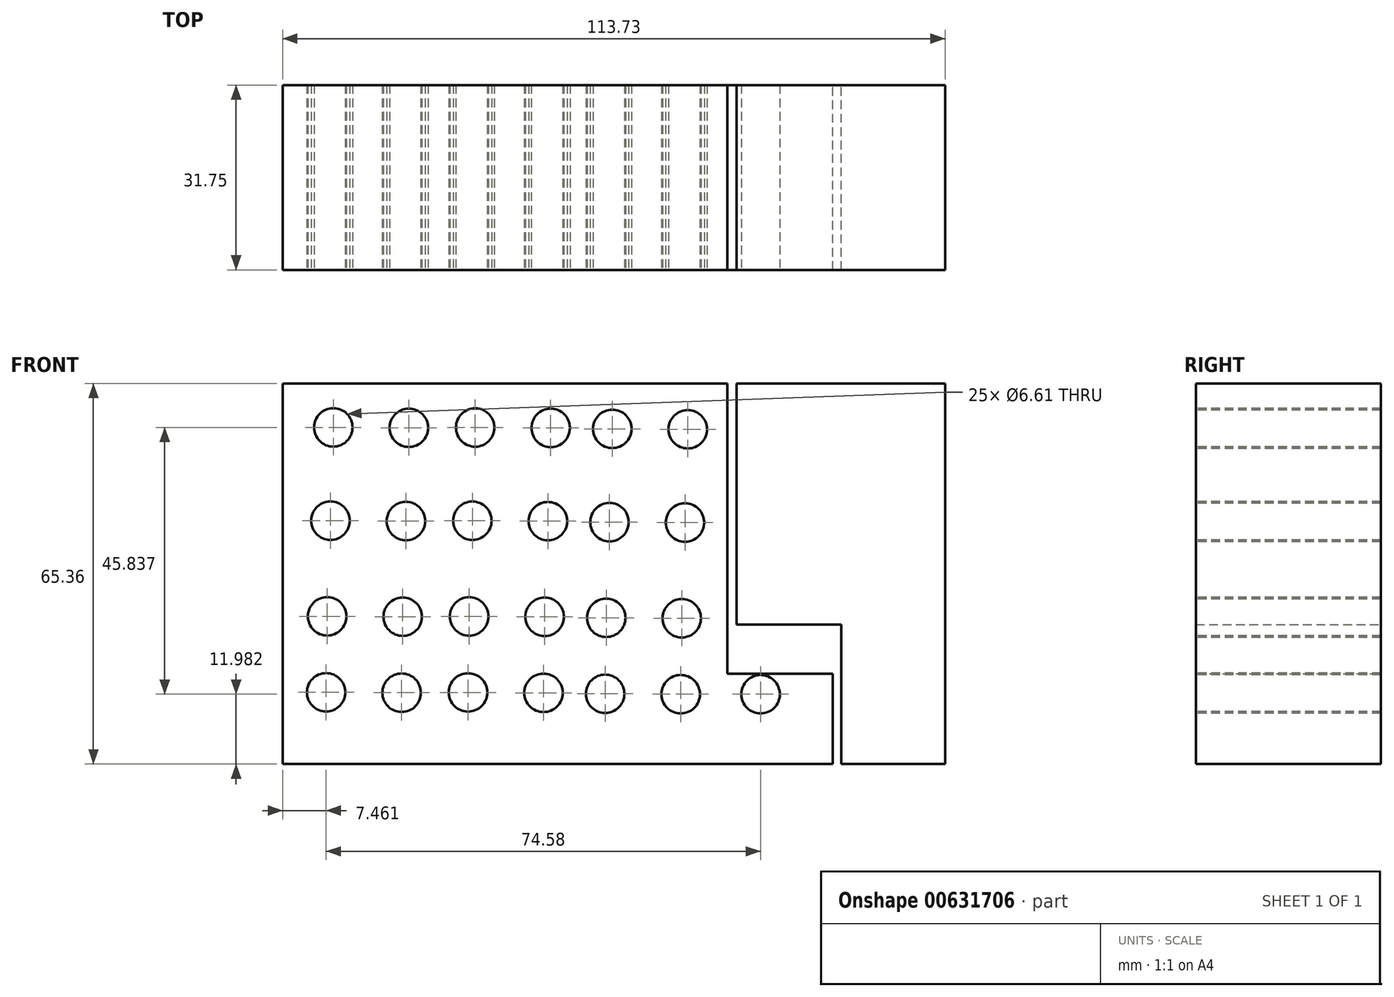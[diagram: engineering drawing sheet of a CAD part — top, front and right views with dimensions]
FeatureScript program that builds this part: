
annotation { "Feature Type Name" : "Feature", "Feature Type Description" : "" }
export const myFeature = defineFeature(function(context is Context, id is Id, definition is map)
    precondition{}
    {
        {
            var Q0;
            Q0=qCreatedBy(makeId("Front.planeOp"),FACE);
            var sketch = newSketch(context, id + "F0", { "sketchPlane" : qUnion([Q0])});
            skLineSegment(sketch, "E0.bottom", {"start": v(0, 0) * mm, "end": v(76.36, 0) * mm});
            skLineSegment(sketch, "E0.top", {"start": v(0, 65.36) * mm, "end": v(76.36, 65.36) * mm});
            skLineSegment(sketch, "E0.left", {"start": v(0, 0) * mm, "end": v(0, 65.36) * mm});
            skLineSegment(sketch, "E0.right", {"start": v(76.36, 0) * mm, "end": v(76.36, 65.36) * mm});
            skLineSegment(sketch, "E1", {"start": v(76.36, 0) * mm, "end": v(95.87, 0) * mm});
            skLineSegment(sketch, "E2", {"start": v(95.87, 0) * mm, "end": v(95.87, 15.7) * mm});
            skLineSegment(sketch, "E3", {"start": v(76.36, 65.36) * mm, "end": v(77.94, 65.36) * mm});
            skLineSegment(sketch, "E4", {"start": v(77.94, 65.36) * mm, "end": v(77.94, 23.98) * mm});
            skLineSegment(sketch, "E5", {"start": v(77.94, 23.98) * mm, "end": v(95.86, 23.98) * mm});
            skLineSegment(sketch, "E6", {"start": v(95.86, 23.98) * mm, "end": v(95.87, 15.7) * mm});
            skLineSegment(sketch, "E7", {"start": v(77.94, 65.36) * mm, "end": v(113.73, 65.36) * mm});
            skLineSegment(sketch, "E8", {"start": v(113.73, 65.36) * mm, "end": v(113.73, 0) * mm});
            skLineSegment(sketch, "E9", {"start": v(113.73, 0) * mm, "end": v(95.87, 0) * mm});
            skLineSegment(sketch, "E10", {"start": v(94.47, 0) * mm, "end": v(94.47, 15.5) * mm});
            skLineSegment(sketch, "E11", {"start": v(94.47, 15.5) * mm, "end": v(76.36, 15.5) * mm});
            skSolve(sketch);
        }
        {
            var Q0;
            {var subQ1=sQuery(id+"F0.wireOp",EDGE,"E0.bottom");Q0=makeQuery(id+"F0.imprint","IMPRINT",FACE,{"disambiguationData":[TD([[makeQuery(id+"F0.imprint","IMPRINT",EDGE,{"derivedFrom":subQ1}),1.0]])]});}
            var Q1;
            {var subQ0=sQuery(id+"F0.wireOp",EDGE,"E1");Q1=makeQuery(id+"F0.imprint","IMPRINT",FACE,{"disambiguationData":[TD([[makeQuery(id+"F0.imprint","IMPRINT",EDGE,{"derivedFrom":subQ0}),1.0]])]});}
            extrude(context, id + "F1", {"entities" : qUnion([Q0, Q1]), "depth" : 31.75 * mm, "offsetDistance" : 25.4 * mm});
        }
        {
            var Q0;
            Q0=makeQuery(id+"F1.opExtrude","CAP_FACE",FACE,{"disambiguationData":[OSD([sQuery(id+"F0.wireOp",EDGE,"E0.bottom"),sQuery(id+"F0.wireOp",EDGE,"E0.top"),sQuery(id+"F0.wireOp",EDGE,"E0.left"),sQuery(id+"F0.wireOp",EDGE,"E0.right"),sQuery(id+"F0.wireOp",EDGE,"E1"),sQuery(id+"F0.wireOp",EDGE,"E2"),sQuery(id+"F0.wireOp",EDGE,"N7w3tQHg-34Xs-ULp0-82r7-44mW0SfcWPOa")])],"isStart":false});
            var sketch = newSketch(context, id + "F2", { "sketchPlane" : qUnion([Q0])});
            skCircle(sketch, "E12", {"center": v(8.7, 57.82) * mm, "radius": 3.3 * mm});
            skCircle(sketch, "E13", {"center": v(21.66, 57.75) * mm, "radius": 3.3 * mm});
            skCircle(sketch, "E14", {"center": v(33.05, 57.8) * mm, "radius": 3.3 * mm});
            skCircle(sketch, "E15", {"center": v(46.02, 57.74) * mm, "radius": 3.3 * mm});
            skCircle(sketch, "E16", {"center": v(56.6, 57.56) * mm, "radius": 3.3 * mm});
            skCircle(sketch, "E17", {"center": v(69.55, 57.5) * mm, "radius": 3.3 * mm});
            skCircle(sketch, "E18", {"center": v(8.2, 41.8) * mm, "radius": 3.3 * mm});
            skCircle(sketch, "E19", {"center": v(21.17, 41.72) * mm, "radius": 3.3 * mm});
            skCircle(sketch, "E20", {"center": v(32.57, 41.78) * mm, "radius": 3.3 * mm});
            skCircle(sketch, "E21", {"center": v(45.53, 41.7) * mm, "radius": 3.3 * mm});
            skCircle(sketch, "E22", {"center": v(56.1, 41.54) * mm, "radius": 3.3 * mm});
            skCircle(sketch, "E23", {"center": v(69.07, 41.47) * mm, "radius": 3.3 * mm});
            skCircle(sketch, "E24", {"center": v(7.65, 25.37) * mm, "radius": 3.3 * mm});
            skCircle(sketch, "E25", {"center": v(20.61, 25.3) * mm, "radius": 3.3 * mm});
            skCircle(sketch, "E26", {"center": v(32.01, 25.35) * mm, "radius": 3.3 * mm});
            skCircle(sketch, "E27", {"center": v(44.97, 25.28) * mm, "radius": 3.3 * mm});
            skCircle(sketch, "E28", {"center": v(55.55, 25.11) * mm, "radius": 3.3 * mm});
            skCircle(sketch, "E29", {"center": v(68.51, 25.04) * mm, "radius": 3.3 * mm});
            skCircle(sketch, "E30", {"center": v(7.46, 12.3) * mm, "radius": 3.3 * mm});
            skCircle(sketch, "E31", {"center": v(20.42, 12.24) * mm, "radius": 3.3 * mm});
            skCircle(sketch, "E32", {"center": v(31.82, 12.3) * mm, "radius": 3.3 * mm});
            skCircle(sketch, "E33", {"center": v(44.79, 12.22) * mm, "radius": 3.3 * mm});
            skCircle(sketch, "E34", {"center": v(55.36, 12.05) * mm, "radius": 3.3 * mm});
            skCircle(sketch, "E35", {"center": v(68.32, 11.98) * mm, "radius": 3.3 * mm});
            skCircle(sketch, "E36", {"center": v(82.04, 11.98) * mm, "radius": 3.3 * mm});
            skSolve(sketch);
        }
        {
            var Q0;
            Q0=makeQuery(id+"F2.imprint","IMPRINT",FACE,{"disambiguationData":[TD([[makeQuery(id+"F2.imprint","IMPRINT",EDGE,{"derivedFrom":sQuery(id+"F2.wireOp",EDGE,"E25")}),1.0]])]});
            var Q1;
            Q1=makeQuery(id+"F2.imprint","IMPRINT",FACE,{"disambiguationData":[TD([[makeQuery(id+"F2.imprint","IMPRINT",EDGE,{"derivedFrom":sQuery(id+"F2.wireOp",EDGE,"E26")}),1.0]])]});
            var Q2;
            Q2=makeQuery(id+"F2.imprint","IMPRINT",FACE,{"disambiguationData":[TD([[makeQuery(id+"F2.imprint","IMPRINT",EDGE,{"derivedFrom":sQuery(id+"F2.wireOp",EDGE,"E27")}),1.0]])]});
            var Q3;
            Q3=makeQuery(id+"F2.imprint","IMPRINT",FACE,{"disambiguationData":[TD([[makeQuery(id+"F2.imprint","IMPRINT",EDGE,{"derivedFrom":sQuery(id+"F2.wireOp",EDGE,"E28")}),1.0]])]});
            var Q4;
            Q4=makeQuery(id+"F2.imprint","IMPRINT",FACE,{"disambiguationData":[TD([[makeQuery(id+"F2.imprint","IMPRINT",EDGE,{"derivedFrom":sQuery(id+"F2.wireOp",EDGE,"E30")}),1.0]])]});
            var Q5;
            Q5=makeQuery(id+"F2.imprint","IMPRINT",FACE,{"disambiguationData":[TD([[makeQuery(id+"F2.imprint","IMPRINT",EDGE,{"derivedFrom":sQuery(id+"F2.wireOp",EDGE,"E32")}),1.0]])]});
            var Q6;
            Q6=makeQuery(id+"F2.imprint","IMPRINT",FACE,{"disambiguationData":[TD([[makeQuery(id+"F2.imprint","IMPRINT",EDGE,{"derivedFrom":sQuery(id+"F2.wireOp",EDGE,"E34")}),1.0]])]});
            var Q7;
            Q7=makeQuery(id+"F2.imprint","IMPRINT",FACE,{"disambiguationData":[TD([[makeQuery(id+"F2.imprint","IMPRINT",EDGE,{"derivedFrom":sQuery(id+"F2.wireOp",EDGE,"E29")}),1.0]])]});
            var Q8;
            Q8=makeQuery(id+"F2.imprint","IMPRINT",FACE,{"disambiguationData":[TD([[makeQuery(id+"F2.imprint","IMPRINT",EDGE,{"derivedFrom":sQuery(id+"F2.wireOp",EDGE,"E31")}),1.0]])]});
            var Q9;
            Q9=makeQuery(id+"F2.imprint","IMPRINT",FACE,{"disambiguationData":[TD([[makeQuery(id+"F2.imprint","IMPRINT",EDGE,{"derivedFrom":sQuery(id+"F2.wireOp",EDGE,"E33")}),1.0]])]});
            var Q10;
            Q10=makeQuery(id+"F2.imprint","IMPRINT",FACE,{"disambiguationData":[TD([[makeQuery(id+"F2.imprint","IMPRINT",EDGE,{"derivedFrom":sQuery(id+"F2.wireOp",EDGE,"E35")}),1.0]])]});
            var Q11;
            Q11=makeQuery(id+"F2.imprint","IMPRINT",FACE,{"disambiguationData":[TD([[makeQuery(id+"F2.imprint","IMPRINT",EDGE,{"derivedFrom":sQuery(id+"F2.wireOp",EDGE,"E24")}),1.0]])]});
            var Q12;
            Q12=makeQuery(id+"F2.imprint","IMPRINT",FACE,{"disambiguationData":[TD([[makeQuery(id+"F2.imprint","IMPRINT",EDGE,{"derivedFrom":sQuery(id+"F2.wireOp",EDGE,"E23")}),1.0]])]});
            var Q13;
            Q13=makeQuery(id+"F2.imprint","IMPRINT",FACE,{"disambiguationData":[TD([[makeQuery(id+"F2.imprint","IMPRINT",EDGE,{"derivedFrom":sQuery(id+"F2.wireOp",EDGE,"E22")}),1.0]])]});
            var Q14;
            Q14=makeQuery(id+"F2.imprint","IMPRINT",FACE,{"disambiguationData":[TD([[makeQuery(id+"F2.imprint","IMPRINT",EDGE,{"derivedFrom":sQuery(id+"F2.wireOp",EDGE,"E21")}),1.0]])]});
            var Q15;
            Q15=makeQuery(id+"F2.imprint","IMPRINT",FACE,{"disambiguationData":[TD([[makeQuery(id+"F2.imprint","IMPRINT",EDGE,{"derivedFrom":sQuery(id+"F2.wireOp",EDGE,"E20")}),1.0]])]});
            var Q16;
            Q16=makeQuery(id+"F2.imprint","IMPRINT",FACE,{"disambiguationData":[TD([[makeQuery(id+"F2.imprint","IMPRINT",EDGE,{"derivedFrom":sQuery(id+"F2.wireOp",EDGE,"E19")}),1.0]])]});
            var Q17;
            Q17=makeQuery(id+"F2.imprint","IMPRINT",FACE,{"disambiguationData":[TD([[makeQuery(id+"F2.imprint","IMPRINT",EDGE,{"derivedFrom":sQuery(id+"F2.wireOp",EDGE,"E18")}),1.0]])]});
            var Q18;
            Q18=makeQuery(id+"F2.imprint","IMPRINT",FACE,{"disambiguationData":[TD([[makeQuery(id+"F2.imprint","IMPRINT",EDGE,{"derivedFrom":sQuery(id+"F2.wireOp",EDGE,"E17")}),1.0]])]});
            var Q19;
            Q19=makeQuery(id+"F2.imprint","IMPRINT",FACE,{"disambiguationData":[TD([[makeQuery(id+"F2.imprint","IMPRINT",EDGE,{"derivedFrom":sQuery(id+"F2.wireOp",EDGE,"E16")}),1.0]])]});
            var Q20;
            Q20=makeQuery(id+"F2.imprint","IMPRINT",FACE,{"disambiguationData":[TD([[makeQuery(id+"F2.imprint","IMPRINT",EDGE,{"derivedFrom":sQuery(id+"F2.wireOp",EDGE,"E15")}),1.0]])]});
            var Q21;
            Q21=makeQuery(id+"F2.imprint","IMPRINT",FACE,{"disambiguationData":[TD([[makeQuery(id+"F2.imprint","IMPRINT",EDGE,{"derivedFrom":sQuery(id+"F2.wireOp",EDGE,"E14")}),1.0]])]});
            var Q22;
            Q22=makeQuery(id+"F2.imprint","IMPRINT",FACE,{"disambiguationData":[TD([[makeQuery(id+"F2.imprint","IMPRINT",EDGE,{"derivedFrom":sQuery(id+"F2.wireOp",EDGE,"E13")}),1.0]])]});
            var Q23;
            Q23=makeQuery(id+"F2.imprint","IMPRINT",FACE,{"disambiguationData":[TD([[makeQuery(id+"F2.imprint","IMPRINT",EDGE,{"derivedFrom":sQuery(id+"F2.wireOp",EDGE,"E12")}),1.0]])]});
            var Q24;
            Q24=makeQuery(id+"F2.imprint","IMPRINT",FACE,{"disambiguationData":[TD([[makeQuery(id+"F2.imprint","IMPRINT",EDGE,{"derivedFrom":sQuery(id+"F2.wireOp",EDGE,"E36")}),1.0]])]});
            var Q25;
            Q25=sQuery(id+"F2.wireOp",EDGE,"E12");
            var Q26;
            Q26=sQuery(id+"F2.wireOp",EDGE,"E18");
            var Q27;
            Q27=sQuery(id+"F2.wireOp",EDGE,"E24");
            var Q28;
            Q28=sQuery(id+"F2.wireOp",EDGE,"E30");
            var Q29;
            Q29=sQuery(id+"F2.wireOp",EDGE,"E31");
            var Q30;
            Q30=sQuery(id+"F2.wireOp",EDGE,"E25");
            var Q31;
            Q31=sQuery(id+"F2.wireOp",EDGE,"E19");
            var Q32;
            Q32=sQuery(id+"F2.wireOp",EDGE,"E13");
            var Q33;
            Q33=sQuery(id+"F2.wireOp",EDGE,"E14");
            var Q34;
            Q34=sQuery(id+"F2.wireOp",EDGE,"E20");
            var Q35;
            Q35=sQuery(id+"F2.wireOp",EDGE,"E26");
            var Q36;
            Q36=sQuery(id+"F2.wireOp",EDGE,"E32");
            var Q37;
            Q37=sQuery(id+"F2.wireOp",EDGE,"E33");
            var Q38;
            Q38=sQuery(id+"F2.wireOp",EDGE,"E27");
            var Q39;
            Q39=sQuery(id+"F2.wireOp",EDGE,"E21");
            var Q40;
            Q40=sQuery(id+"F2.wireOp",EDGE,"E15");
            var Q41;
            Q41=sQuery(id+"F2.wireOp",EDGE,"E16");
            var Q42;
            Q42=sQuery(id+"F2.wireOp",EDGE,"E22");
            var Q43;
            Q43=sQuery(id+"F2.wireOp",EDGE,"E28");
            var Q44;
            Q44=sQuery(id+"F2.wireOp",EDGE,"E34");
            var Q45;
            Q45=sQuery(id+"F2.wireOp",EDGE,"E35");
            var Q46;
            Q46=sQuery(id+"F2.wireOp",EDGE,"E29");
            var Q47;
            Q47=sQuery(id+"F2.wireOp",EDGE,"E23");
            var Q48;
            Q48=sQuery(id+"F2.wireOp",EDGE,"E17");
            extrude(context, id + "F3", {"entities" : qUnion([Q0, Q1, Q2, Q3, Q4, Q5, Q6, Q7, Q8, Q9, Q10, Q11, Q12, Q13, Q14, Q15, Q16, Q17, Q18, Q19, Q20, Q21, Q22, Q23, Q24]), "operationType" : NewBodyOperationType.REMOVE, "surfaceEntities" : qUnion([Q25, Q26, Q27, Q28, Q29, Q30, Q31, Q32, Q33, Q34, Q35, Q36, Q37, Q38, Q39, Q40, Q41, Q42, Q43, Q44, Q45, Q46, Q47, Q48]), "oppositeDirection" : true, "depth" : 37.6 * mm, "offsetDistance" : 25.4 * mm});
        }
        {
            var Q0;
            Q0=makeQuery(id+"F0.imprint","IMPRINT",FACE,{"disambiguationData":[TD([[makeQuery(id+"F0.imprint","IMPRINT",EDGE,{"derivedFrom":sQuery(id+"F0.wireOp",EDGE,"E2")}),-1.0]])]});
            extrude(context, id + "F4", {"entities" : qUnion([Q0]), "depth" : 31.75 * mm, "offsetDistance" : 25.4 * mm});
        }
    });
